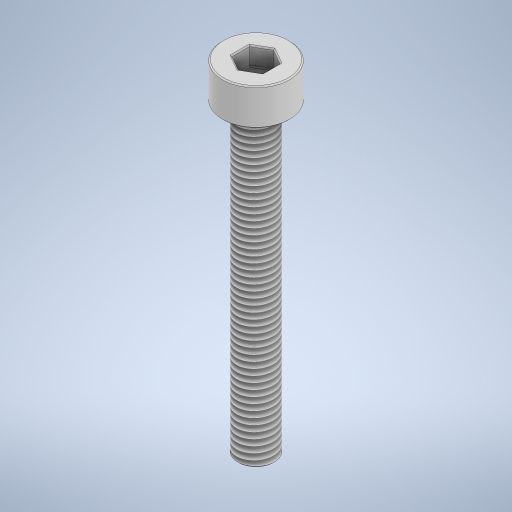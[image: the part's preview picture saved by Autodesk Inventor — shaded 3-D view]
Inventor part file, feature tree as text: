
AUTODESK INVENTOR PART (.ipt)
format: ipt  version: 2023 (Build 270158000, 158)  size: 314,880 bytes
history: native  units: in
note: dims shown in document units (in); Inventor stores cm internally (conversion verified against a paired STEP export)
features: sketch x2, revolve x1, thread x1, extrude x1, chamfer x1
ambient origin geometry x8: Origin, YZ Plane, XZ Plane, XY Plane, X Axis, Y Axis, Z Axis, Center Point
bodies: Solid1 (feature_tree)
feature tree (6):
  revolve  "Revolution1"  [1 undecoded]
  thread  "Thread1"  [1 undecoded]
  extrude  "Extrusion2"  TaperAngle=90.0deg  [1 undecoded]
  chamfer  "Chamfer2"  Distance=0.1181in
  sketch  "Sketch1"  dims[d0=0.1083in d1=0.1181in d2=0.9843in]
  sketch  "Sketch3"  dims[d3=0.0591in d4=90.0deg d5=0.1181in d6=0.0in d13=0.0984in d14=0.0591in d15=0.0in d16=0.0039in d17=0.0787in d18=45.0deg]
note: 3 required parameter values undecoded (feature->parameter linkage not recoverable at this tier; creation-order binding heuristic only, values carry confidence <= 0.55)